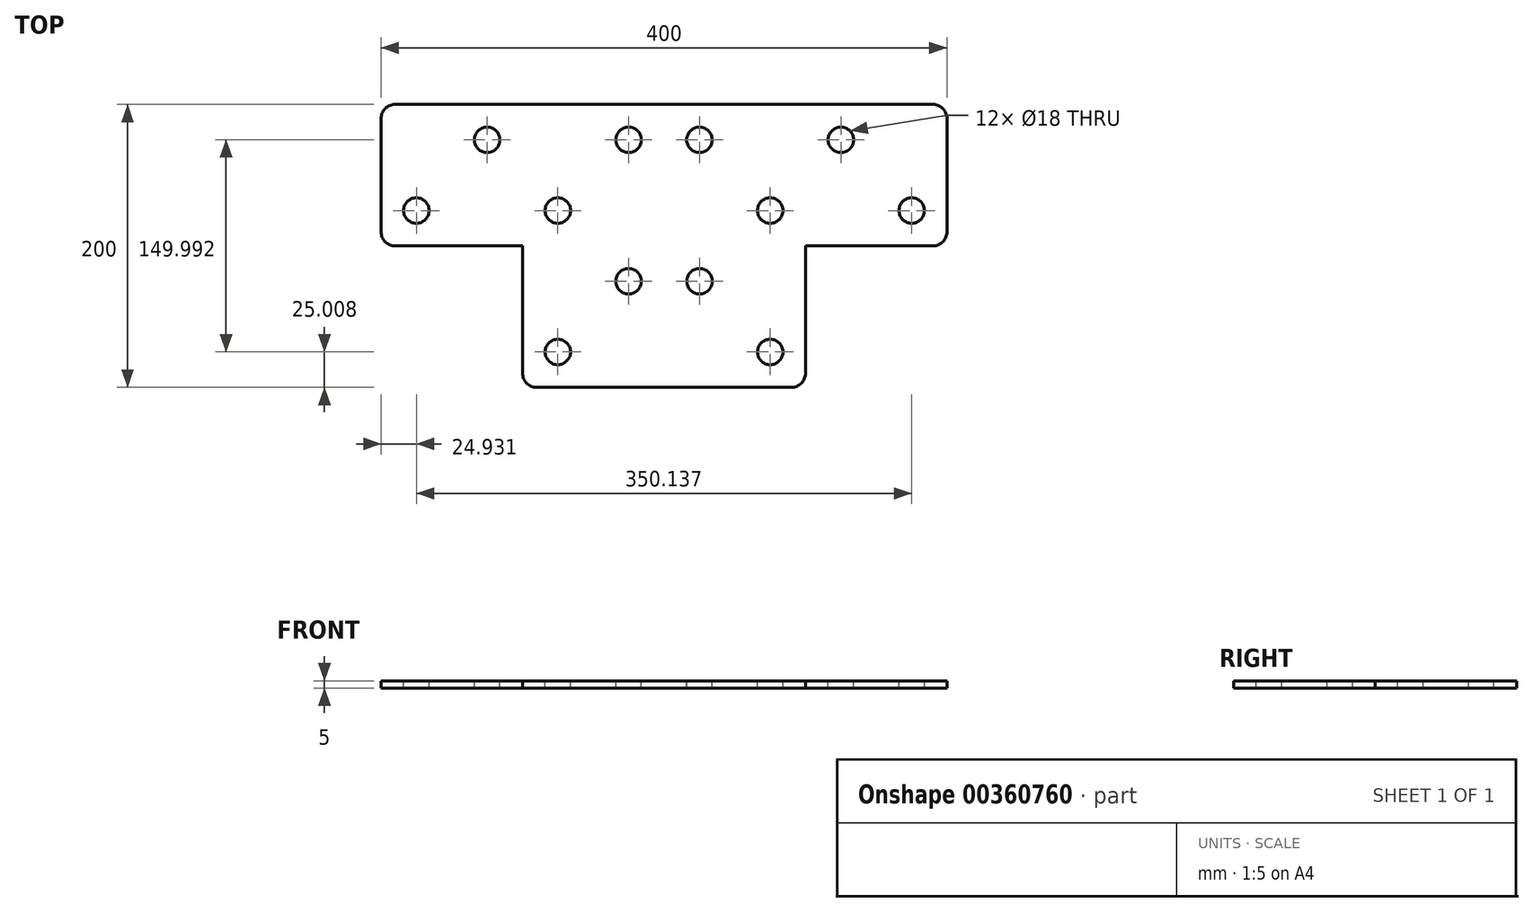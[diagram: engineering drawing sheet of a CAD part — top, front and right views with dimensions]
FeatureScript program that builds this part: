
annotation { "Feature Type Name" : "Feature", "Feature Type Description" : "" }
export const myFeature = defineFeature(function(context is Context, id is Id, definition is map)
    precondition{}
    {
        {
            var Q0;
            Q0=qCreatedBy(makeId("Top.planeOp"),FACE);
            var sketch = newSketch(context, id + "F0", { "sketchPlane" : qUnion([Q0])});
            skLineSegment(sketch, "E0", {"start": v(0, 0) * mm, "end": v(200, 0) * mm});
            skLineSegment(sketch, "E1", {"start": v(200, 0) * mm, "end": v(200, -100) * mm});
            skLineSegment(sketch, "E2", {"start": v(200, -100) * mm, "end": v(100, -100) * mm});
            skLineSegment(sketch, "E3", {"start": v(100, -100) * mm, "end": v(100, -200) * mm});
            skLineSegment(sketch, "E4", {"start": v(100, -200) * mm, "end": v(0, -200) * mm});
            skLineSegment(sketch, "E5.MirrorCS", {"start": v(0, 0) * mm, "end": v(-200, 0) * mm});
            skLineSegment(sketch, "E6.MirrorCS", {"start": v(-200, 0) * mm, "end": v(-200, -100) * mm});
            skLineSegment(sketch, "E7.MirrorCS", {"start": v(-200, -100) * mm, "end": v(-100, -100) * mm});
            skLineSegment(sketch, "E8.MirrorCS", {"start": v(-100, -100) * mm, "end": v(-100, -200) * mm});
            skLineSegment(sketch, "E9.MirrorCS", {"start": v(-100, -200) * mm, "end": v(0, -200) * mm});
            skSolve(sketch);
        }
        {
            var Q0;
            Q0=makeQuery(id+"F0.imprint","IMPRINT",FACE,{"disambiguationData":[TD([[makeQuery(id+"F0.imprint","IMPRINT",EDGE,{"derivedFrom":sQuery(id+"F0.wireOp",EDGE,"E0")}),-1.0]])]});
            extrude(context, id + "F1", {"entities" : qUnion([Q0]), "depth" : 5 * mm});
        }
        {
            var Q0;
            Q0=makeQuery(id+"F1.opExtrude","CAP_FACE",FACE,{"disambiguationData":[OSD([sQuery(id+"F0.wireOp",EDGE,"E0"),sQuery(id+"F0.wireOp",EDGE,"E1"),sQuery(id+"F0.wireOp",EDGE,"E2"),sQuery(id+"F0.wireOp",EDGE,"E3"),sQuery(id+"F0.wireOp",EDGE,"E4"),sQuery(id+"F0.wireOp",EDGE,"E5.MirrorCS"),sQuery(id+"F0.wireOp",EDGE,"E6.MirrorCS"),sQuery(id+"F0.wireOp",EDGE,"E7.MirrorCS"),sQuery(id+"F0.wireOp",EDGE,"E8.MirrorCS"),sQuery(id+"F0.wireOp",EDGE,"E9.MirrorCS")])],"isStart":false});
            var sketch = newSketch(context, id + "F2", { "sketchPlane" : qUnion([Q0])});
            skPoint(sketch, "E10.startSnap0", {"position": v(175.07, -50) * mm});
            skCircle(sketch, "E11.MirrorC", {"center": v(175.07, -75) * mm, "radius": 9 * mm});
            skCircle(sketch, "E12.MirrorC", {"center": v(125, -25) * mm, "radius": 9 * mm});
            skCircle(sketch, "E13.MirrorC", {"center": v(75.07, -75) * mm, "radius": 9 * mm});
            skCircle(sketch, "E14.MirrorC", {"center": v(75.07, -175) * mm, "radius": 9 * mm});
            skCircle(sketch, "E15.MirrorC", {"center": v(25.07, -125) * mm, "radius": 9 * mm});
            skCircle(sketch, "E16.MirrorC", {"center": v(25, -25) * mm, "radius": 9 * mm});
            skPoint(sketch, "E17.MirrorP", {"position": v(-175.07, -50) * mm});
            skCircle(sketch, "E18.MirrorC", {"center": v(-75.07, -175) * mm, "radius": 9 * mm});
            skCircle(sketch, "E19.MirrorC", {"center": v(-25, -25) * mm, "radius": 9 * mm});
            skCircle(sketch, "E20.MirrorC", {"center": v(-175.07, -75) * mm, "radius": 9 * mm});
            skCircle(sketch, "E21.MirrorC", {"center": v(-125, -25) * mm, "radius": 9 * mm});
            skCircle(sketch, "E22.MirrorC", {"center": v(-75.07, -75) * mm, "radius": 9 * mm});
            skCircle(sketch, "E23.MirrorC", {"center": v(-25.07, -125) * mm, "radius": 9 * mm});
            skSolve(sketch);
        }
        {
            var Q0;
            Q0=qSketchRegion(id+"F2",true);
            extrude(context, id + "F3", {"entities" : qUnion([Q0]), "operationType" : NewBodyOperationType.REMOVE, "oppositeDirection" : true, "depth" : 25 * mm});
        }
        {
            var Q0;
            Q0=makeQuery(id+"F1.opExtrude","SWEPT_EDGE",EDGE,{"disambiguationData":[OSD([sQuery(id+"F0.wireOp",EDGE,"E8.MirrorCS"),sQuery(id+"F0.wireOp",EDGE,"E9.MirrorCS")])]});
            var Q1;
            Q1=makeQuery(id+"F1.opExtrude","SWEPT_EDGE",EDGE,{"disambiguationData":[OSD([sQuery(id+"F0.wireOp",EDGE,"E3"),sQuery(id+"F0.wireOp",EDGE,"E4")])]});
            var Q2;
            Q2=makeQuery(id+"F1.opExtrude","SWEPT_EDGE",EDGE,{"disambiguationData":[OSD([sQuery(id+"F0.wireOp",EDGE,"E1"),sQuery(id+"F0.wireOp",EDGE,"E2")])]});
            var Q3;
            Q3=makeQuery(id+"F1.opExtrude","SWEPT_EDGE",EDGE,{"disambiguationData":[OSD([sQuery(id+"F0.wireOp",EDGE,"E0"),sQuery(id+"F0.wireOp",EDGE,"E1")])]});
            var Q4;
            Q4=makeQuery(id+"F1.opExtrude","SWEPT_EDGE",EDGE,{"disambiguationData":[OSD([sQuery(id+"F0.wireOp",EDGE,"E6.MirrorCS"),sQuery(id+"F0.wireOp",EDGE,"E7.MirrorCS")])]});
            var Q5;
            Q5=makeQuery(id+"F1.opExtrude","SWEPT_EDGE",EDGE,{"disambiguationData":[OSD([sQuery(id+"F0.wireOp",EDGE,"E5.MirrorCS"),sQuery(id+"F0.wireOp",EDGE,"E6.MirrorCS")])]});
            fillet(context, id + "F4", {"entities" : qUnion([Q0, Q1, Q2, Q3, Q4, Q5]), "radius" : 10 * mm, "tangentPropagation" : true, "allowEdgeOverflow" : false});
        }
    });
